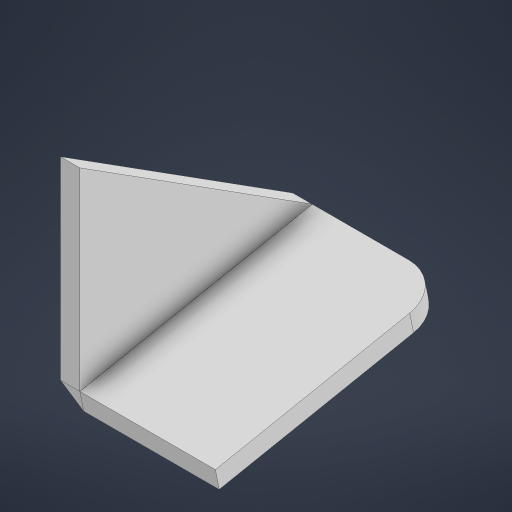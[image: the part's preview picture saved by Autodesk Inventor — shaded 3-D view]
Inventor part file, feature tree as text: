
AUTODESK INVENTOR PART (.ipt)
format: ipt  version: 2023 (Build 270158000, 158)  size: 196,608 bytes
history: native  units: in
note: dims shown in document units (in); Inventor stores cm internally (conversion verified against a paired STEP export)
features: extrude x2, sketch x2, other x2, loft x1, fillet x1
ambient origin geometry x8: Origin, YZ Plane, XZ Plane, XY Plane, X Axis, Y Axis, Z Axis, Center Point
bodies: Solid1 (feature_tree), Solid2 (feature_tree)
feature tree (8):
  extrude  "Extrusion1"  Depth=0.5in TaperAngle=0.0deg
  extrude  "Extrusion2"  Depth=1.0in
  loft  "Loft1"
  fillet  "Fillet1"  [1 undecoded]
  sketch  "Sketch1"  dims[d0=5.0in d2=0.5in d3=0.0in]
  sketch  "Sketch2"  dims[d5=0.077in d6=6.0in d7=0.0in d8=0.0in d9=3.5in d10=0.5in d11=0.0in d12=0.0in d13=90.0deg d14=0.0in d15=90.0deg d16=1.0in]
  other  "Edges1"
  other  "Edges2"
note: 1 required parameter value undecoded (feature->parameter linkage not recoverable at this tier; creation-order binding heuristic only, values carry confidence <= 0.55)
